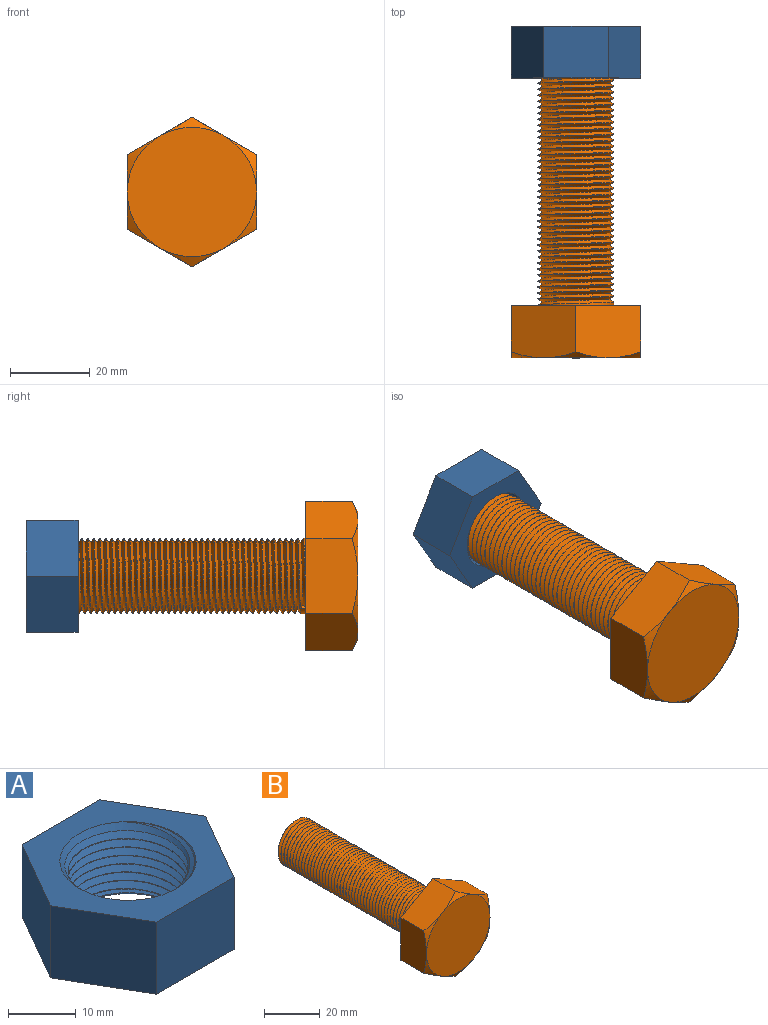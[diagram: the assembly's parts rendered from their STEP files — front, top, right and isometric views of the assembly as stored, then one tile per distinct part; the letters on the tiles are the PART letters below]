
ASSEMBLY  parts=2 mates=2
PART A: 13 faces, bbox 32.3x28x14.7 mm
  f0: plane 14x13mm, normal (-0.87,-0.5,0), area 210.2mm2, adj f1,f6,f7,f8
  f1: plane 16.17x13mm, normal (0,-1,0), area 210.2mm2, adj f0,f2,f7,f8
  f2: plane 14x13mm, normal (0.87,-0.5,0), area 210.2mm2, adj f1,f3,f7,f8
  f3: plane 14x13mm, normal (0.87,0.5,0), area 210.2mm2, adj f2,f4,f7,f8
  f4: plane 16.17x13mm, normal (0,1,0), area 210.2mm2, adj f3,f6,f7,f8
  f5: cylinder r=8.84mm len=17.68mm, axis (0,0,-1), area 21.8mm2, adj f9,f10,f11,f12
  f6: plane 14x13mm, normal (-0.87,0.5,0), area 210.2mm2, adj f0,f4,f7,f8
  f7: plane 32.33x28mm, normal (0,0,1), area 362.4mm2, adj f0,f1,f2,f3,f4,f6,f10,f11
  f8: plane 32.33x28mm, normal (0,0,-1), area 362.4mm2, adj f0,f1,f2,f3,f4,f6,f9,f11
  f9: cone r=10.04mm half-angle=45deg, axis (0,0,-1), area 54mm2, adj f5,f8,f11,f12
  f10: cone r=8.84mm half-angle=45deg, axis (0,0,1), area 54.3mm2, adj f5,f7,f11,f12
  f11: bspline ~23.21x20.1mm, area 656.1mm2, adj f5,f7,f8,f9,f10,f12
  f12: bspline ~23.21x20.1mm, area 654.3mm2, adj f5,f7,f8,f9,f10,f11
PART B: 19 faces, bbox 38.9x85.4x38.9 mm
  f0: cylinder r=9.5mm len=70mm, axis (0,-1,0), area 1545.6mm2, adj f1,f2,f3,f4,f5
  f1: plane 18.95x18.93mm, normal (0,1,0), area 251.2mm2, adj f0,f2,f3
  f2: bspline ~70.45x21.94mm, area 3620mm2, adj f0,f1,f3,f4
  f3: bspline ~70.95x21.94mm, area 3637.7mm2, adj f0,f1,f2,f4,f5
  f4: plane 1.4x1.05mm, normal (-0.87,0,0.5), area 0.8mm2, adj f0,f2,f3
  f5: plane 37.33x32.33mm, normal (0,1,0), area 621.8mm2, adj f0,f3,f6,f7,f8,f9,f10,f11
  f6: plane 20.22x14.55mm, normal (-1,0,0), area 233.4mm2, adj f5,f7,f11,f12,f17
  f7: plane 17.7x14.54mm, normal (-0.5,0,-0.87), area 233.4mm2, adj f5,f6,f8,f16,f17
  f8: plane 17.7x14.54mm, normal (0.5,0,-0.87), area 233.4mm2, adj f5,f7,f9,f15,f16
  f9: plane 20.22x14.55mm, normal (1,0,0), area 233.4mm2, adj f5,f8,f10,f14,f15
  f10: plane 17.7x14.54mm, normal (0.5,0,0.87), area 233.4mm2, adj f5,f9,f11,f13,f14
  f11: plane 17.7x14.54mm, normal (-0.5,0,0.87), area 233.4mm2, adj f5,f6,f10,f12,f13
  f12: cone r=27.72mm half-angle=60deg, axis (0,1,0), area 25.7mm2, adj f6,f11,f18
  f13: cone r=27.72mm half-angle=60deg, axis (0,1,0), area 25.7mm2, adj f10,f11,f18
  f14: cone r=27.72mm half-angle=60deg, axis (0,1,0), area 25.7mm2, adj f9,f10,f18
  f15: cone r=27.72mm half-angle=60deg, axis (0,1,0), area 25.7mm2, adj f8,f9,f18
  f16: cone r=27.72mm half-angle=60deg, axis (0,1,0), area 25.7mm2, adj f7,f8,f18
  f17: cone r=27.72mm half-angle=60deg, axis (0,1,0), area 25.7mm2, adj f6,f7,f18
  f18: plane 32.33x32.33mm, normal (0,-1,0), area 821mm2, adj f12,f13,f14,f15,f16,f17
PLACE A rot(axis=(1,0,0),90deg) t=(-52.68,-57.69,8.82)mm
PLACE B t=(-52.7,-127.69,8.92)mm
MATE parallel A.f7 <-> B.f0  axis (0,-1,0) through (-46.12,-70.69,16.41)mm
MATE pin_slot A.f5 <-> B.f1  axis (0,1,0) through (-52.68,-57.69,8.82)mm
